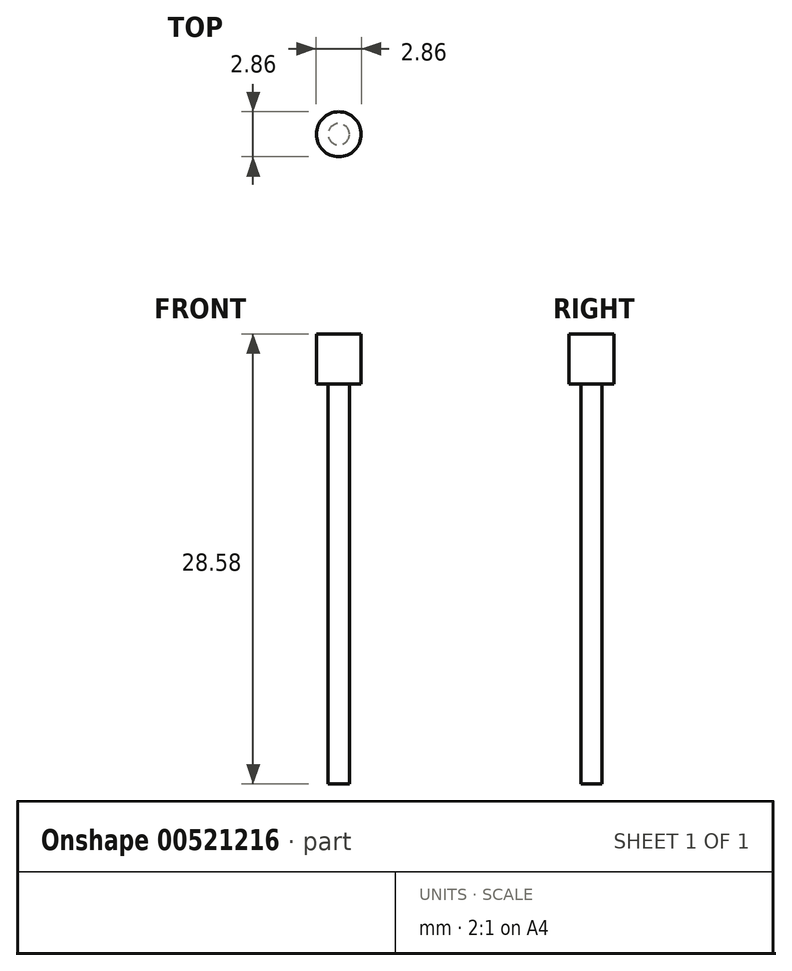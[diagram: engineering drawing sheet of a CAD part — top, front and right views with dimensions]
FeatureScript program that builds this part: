
annotation { "Feature Type Name" : "Feature", "Feature Type Description" : "" }
export const myFeature = defineFeature(function(context is Context, id is Id, definition is map)
    precondition{}
    {
        {
            var Q0;
            Q0=qCreatedBy(makeId("Top.planeOp"),FACE);
            var sketch = newSketch(context, id + "F0", { "sketchPlane" : qUnion([Q0])});
            skCircle(sketch, "E0", {"center": v(0, 0) * mm, "radius": 0.68 * mm});
            skSolve(sketch);
        }
        {
            var Q0;
            Q0 = qSketchRegion(id + "F0", true);
            extrude(context, id + "F1", {"entities" : qUnion([Q0]), "oppositeDirection" : true, "depth" : 25.4 * mm, "offsetDistance" : 25.4 * mm});
        }
        {
            var Q0;
            Q0=qCreatedBy(makeId("Top.planeOp"),FACE);
            var sketch = newSketch(context, id + "F2", { "sketchPlane" : qUnion([Q0])});
            skCircle(sketch, "E1", {"center": v(0, 0) * mm, "radius": 1.43 * mm});
            skSolve(sketch);
        }
        {
            var Q0;
            Q0 = qSketchRegion(id + "F2", true);
            extrude(context, id + "F3", {"entities" : qUnion([Q0]), "operationType" : NewBodyOperationType.ADD, "depth" : 3.17 * mm, "offsetDistance" : 25.4 * mm});
        }
    });
